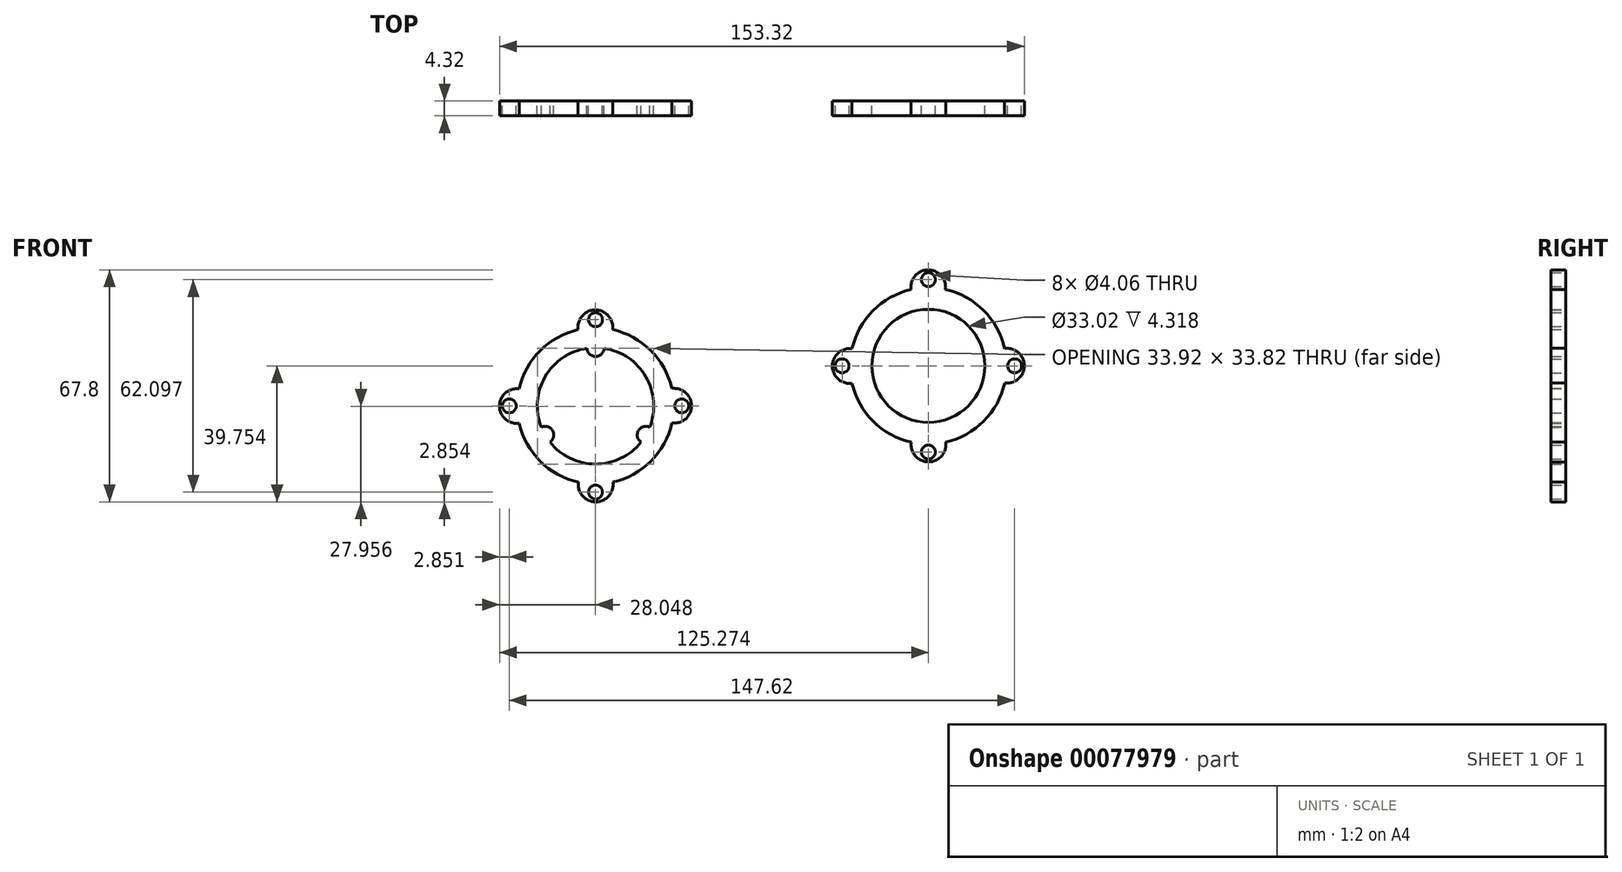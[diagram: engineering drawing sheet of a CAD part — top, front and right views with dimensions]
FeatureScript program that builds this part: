
annotation { "Feature Type Name" : "Feature", "Feature Type Description" : "" }
export const myFeature = defineFeature(function(context is Context, id is Id, definition is map)
    precondition{}
    {
        {
            var Q0;
            Q0=qCreatedBy(makeId("Front.planeOp"),FACE);
            var sketch = newSketch(context, id + "F0", { "sketchPlane" : qUnion([Q0])});
            skArc(sketch, "E0", {"start": v(-75.76, 15.34) * mm, "mid": v(-69.6, 4.22) * mm, "end": v(-58.46, -1.89) * mm});
            skLineSegment(sketch, "E1", {"start": v(-53.47, 43.28) * mm, "end": v(-53.47, 45.62) * mm});
            skCircle(sketch, "E2", {"center": v(-53.47, 45.62) * mm, "radius": 2.03 * mm});
            skArc(sketch, "E3", {"start": v(-48.48, 42.73) * mm, "mid": v(-53.53, 48.47) * mm, "end": v(-58.55, 42.7) * mm});
            skCircle(sketch, "E4.1.0", {"center": v(-78.67, 20.42) * mm, "radius": 2.03 * mm});
            skArc(sketch, "E4.1.1", {"start": v(-75.78, 25.41) * mm, "mid": v(-81.52, 20.37) * mm, "end": v(-75.76, 15.34) * mm});
            skCircle(sketch, "E4.2.0", {"center": v(-53.47, -4.78) * mm, "radius": 2.03 * mm});
            skArc(sketch, "E4.2.1", {"start": v(-58.46, -1.89) * mm, "mid": v(-53.42, -7.63) * mm, "end": v(-48.4, -1.87) * mm});
            skCircle(sketch, "E4.3.0", {"center": v(-28.28, 20.42) * mm, "radius": 2.03 * mm});
            skArc(sketch, "E4.3.1", {"start": v(-31.16, 15.43) * mm, "mid": v(-25.42, 20.48) * mm, "end": v(-31.18, 25.5) * mm});
            skArc(sketch, "E5", {"start": v(-37.64, 14.2) * mm, "mid": v(-38.75, 28.92) * mm, "end": v(-50.94, 37.24) * mm});
            skArc(sketch, "E6", {"start": v(38.67, 54.41) * mm, "mid": v(27.56, 48.26) * mm, "end": v(21.45, 37.11) * mm});
            skLineSegment(sketch, "E7", {"start": v(43.75, 54.98) * mm, "end": v(43.75, 57.32) * mm});
            skCircle(sketch, "E8", {"center": v(43.75, 57.32) * mm, "radius": 2.03 * mm});
            skArc(sketch, "E9", {"start": v(48.74, 54.43) * mm, "mid": v(43.7, 60.17) * mm, "end": v(38.67, 54.41) * mm});
            skCircle(sketch, "E10.1.0", {"center": v(18.56, 32.12) * mm, "radius": 2.03 * mm});
            skArc(sketch, "E10.1.1", {"start": v(21.45, 37.11) * mm, "mid": v(15.7, 32.07) * mm, "end": v(21.47, 27.04) * mm});
            skCircle(sketch, "E10.2.0", {"center": v(43.75, 6.93) * mm, "radius": 2.03 * mm});
            skArc(sketch, "E10.2.1", {"start": v(38.76, 9.82) * mm, "mid": v(43.81, 4.07) * mm, "end": v(48.83, 9.84) * mm});
            skCircle(sketch, "E10.3.0", {"center": v(68.95, 32.12) * mm, "radius": 2.03 * mm});
            skArc(sketch, "E10.3.1", {"start": v(66.06, 27.13) * mm, "mid": v(71.8, 32.18) * mm, "end": v(66.04, 37.2) * mm});
            skCircle(sketch, "E11", {"center": v(43.75, 32.12) * mm, "radius": 16.51 * mm});
            skArc(sketch, "E12", {"start": v(-56, 37.24) * mm, "mid": v(-53.47, 34.89) * mm, "end": v(-50.94, 37.24) * mm});
            skArc(sketch, "E13.1.0", {"start": v(-66.77, 9.82) * mm, "mid": v(-66, 13.19) * mm, "end": v(-69.3, 14.2) * mm});
            skArc(sketch, "E13.2.0", {"start": v(-37.64, 14.2) * mm, "mid": v(-40.95, 13.19) * mm, "end": v(-40.18, 9.82) * mm});
            skArc(sketch, "E14.trimOffspring", {"start": v(-66.77, 9.82) * mm, "mid": v(-53.47, 3.42) * mm, "end": v(-40.18, 9.82) * mm});
            skArc(sketch, "E15.trimOffspring", {"start": v(-56, 37.24) * mm, "mid": v(-68.2, 28.92) * mm, "end": v(-69.3, 14.2) * mm});
            skArc(sketch, "E16.trimOffspring", {"start": v(-48.4, -1.87) * mm, "mid": v(-37.28, 4.29) * mm, "end": v(-31.16, 15.43) * mm});
            skArc(sketch, "E17.trimOffspring", {"start": v(-31.18, 25.5) * mm, "mid": v(-37.34, 36.62) * mm, "end": v(-48.48, 42.73) * mm});
            skArc(sketch, "E18.trimOffspring", {"start": v(-58.55, 42.7) * mm, "mid": v(-69.67, 36.55) * mm, "end": v(-75.78, 25.41) * mm});
            skArc(sketch, "E19.trimOffspring", {"start": v(21.47, 27.04) * mm, "mid": v(27.62, 15.93) * mm, "end": v(38.76, 9.82) * mm});
            skArc(sketch, "E20.trimOffspring", {"start": v(48.83, 9.84) * mm, "mid": v(59.95, 16) * mm, "end": v(66.06, 27.13) * mm});
            skArc(sketch, "E21.trimOffspring", {"start": v(66.04, 37.2) * mm, "mid": v(59.89, 48.32) * mm, "end": v(48.74, 54.43) * mm});
            skSolve(sketch);
        }
        {
            var Q0;
            Q0 = qSketchRegion(id + "F0", true);
            extrude(context, id + "F1", {"entities" : qUnion([Q0]), "depth" : 4.32 * mm});
        }
    });
